# Revit family: Legrand_Hotel_UX_TOUCH_Motion_Sensor
name_source: partatom
category: Equipement électrique
units: mm (PartAtom-declared; Revit-internal decimal feet)

## family parameters
Configuration du panneau = Deux colonnes, circuits au sein
Cote de connecteur circulaire = Utiliser le diamètre
Couper avec des vides une fois chargée = Non
Hôte = Face
Partagée = Non
Point de calcul de pièce = Non
Type d'élément = Tableau de raccordement

## types (1)
- Motion Sensor
    Alarm function = Non
    Colour = white
    Constant light control = Non
    Degree of protection (IP) = IP42
    Description = Movement detector
    Diameter detection range on floor = 5 mm  [stored 0.0164042 ft]
    Dim function with dimmer basic element = Non
    Elévation par défaut = 2500 mm  [stored 8.2021 ft]
    Fabricant = Legrand
    Forced switch off = Non
    General Conditions of Use = https://export.legrand.com
    HVAC-control = Non
    Material = LEGRAND -  White plastic
    Max. switching power = 0,3
    Model = Movement sensor
    Modèle = 048778
    Mounting method = Flush mounted (plaster)
    Nominal voltage (V) = 12
    Optimum mounting height = 3 mm  [stored 0.00984252 ft]
    Overall height = 38 mm  [stored 0.124672 ft]
    Overall width = 38 mm  [stored 0.124672 ft]
    RAL-number (akin) = 9003
    Remote operation = Non
    Response value luminosity adjustable = Non
    Response value sensitivity adjustable = Non
    Sensor type = Passive infrared
    Substation input = Non
    Suitable for wireless transmission = Non
    Temperature MIN-MAX (°C) = -5-45
    URL = http://www.legrandoc.com
    Voltage type = DC

note: [stored X ft] marks values corroborated as IEEE doubles in the binary element streams (Revit-internal decimal feet)
